# Revit family: 120908-00184  Шкаф распределительный телефонный ШР-600-2М (пустой) ССД
name_source: partatom
category: Обобщенные модели
units: mm (PartAtom-declared; Revit-internal decimal feet)

## family parameters
Всегда вертикально = Да
Может служить основой для арматурных стержней = Нет
На основе рабочей плоскости = Нет
Общий = Нет
При загрузке вырезать с полостями = Нет
Размер круглого соединителя = Использовать диаметр
Тип детали = Нормальный
Точка расчета площади = Нет

## types (1)
- ШР-600-2М
    ADSK_URL документации изделия = shr_decl_2017.pdf (ssd.ru)
    ADSK_URL страницы изделия = Шкаф распределительный телефонный ШР-600-2М (пустой) ССД ( 120908-00184 ) (ssd.ru)
    ADSK_Единица измерения = шт
    ADSK_Завод-изготовитель = АО СВЯЗЬСТРОЙДЕТАЛЬ
    ADSK_Код изделия = 120908-00184
    ADSK_Масса_Текст = 74
    ADSK_Наименование = Шкаф распределительный телефонный ШР-600-2М (пустой) ССД
    ADSK_Наименование краткое = ШР-600-2М
    ADSK_Размер_Высота = 1550 мм
    ADSK_Размер_Глубина = 285 мм
    ADSK_Размер_Ширина = 640 мм
    Материал Каркаса = Металл серый
    Материал букв = Металл красный
    Ноль = 0 мм
    Описание = Шкаф распределительный телефонный ШР-600-2М (пустой) ССД
    Толщина -4 = -4 мм
    Толщина 25 = 25 мм
    Толщина 4 = 4 мм
    Толщина 5 = 5 мм

## geometry (parser evidence)
native form markers: Blend x2
no freeform markers — native parametric forms only
